# Revit family: Electronics_Commercial-Audio_Biamp_Stereo-Preamplifier_PREZONE-2
name_source: partatom
category: Communication Devices
units: mm (PartAtom-declared; Revit-internal decimal feet)

## family parameters
Cut with Voids When Loaded = No
Host = Face
Maintain Annotation Orientation = No
OmniClass Number = 23.85.10.11.14
OmniClass Title = Audio Equipment
Part Type = Normal
Room Calculation Point = No
Round Connector Dimension = Use Diameter
Shared = No

## types (1)
- PREZONE2
    Altitude = 0-6,600 ft (0-2000m) MSL
    Apparent Load = 60 VA
    Colling = Convection
    Compliance = FCC Part 15B (USA)
UL listed (USA and Canada)
CE Marked (Europe)
RoHS Directive (Europe)
    Connector Description = 250V DC 60W
    Default Elevation = 4' - 0"
    Depth = 0' - 11 13/32"
    Description = PREZONE2 Stereo Preamplifier
    Emergency input = Yes
    Frequency response (in Hz) = 20 Hz - 20 kHz
    Height = 0' - 3 1/2"
    Housing Material = Biamp - Metal - Black
    Humidity = 0-95% relative humidity (non-condensing)
    Line input unbalanced = 2
    MIC inputs balanced = 2
    MIC level control = Yes
    Manufacturer = Biamp
    Max Power Consumption = 60 W
    Model = PREZONE2
    Music level control = Yes
    Power Factor = 1
    Prioriti levels = 4
    Product Documentation Link = https://downloads.biamp.com
    Product Page URL = https://www.biamp.com
    Product data url = https://www.bimobject.com
    RS232 = 115200/8-N-1
    Source selection per zone = Yes
    Temperature Range = 32 - 104° F (0 – 40° C)
    Tone control = Yes
    URL = https://www.biamp.com
    VOX mute = Yes
    Voltage = 120 V
    Weight = 8.60 lbf
    Width = 1' - 4 15/16"

## geometry (parser evidence)
native form markers: Sweep x3
no freeform markers — native parametric forms only
